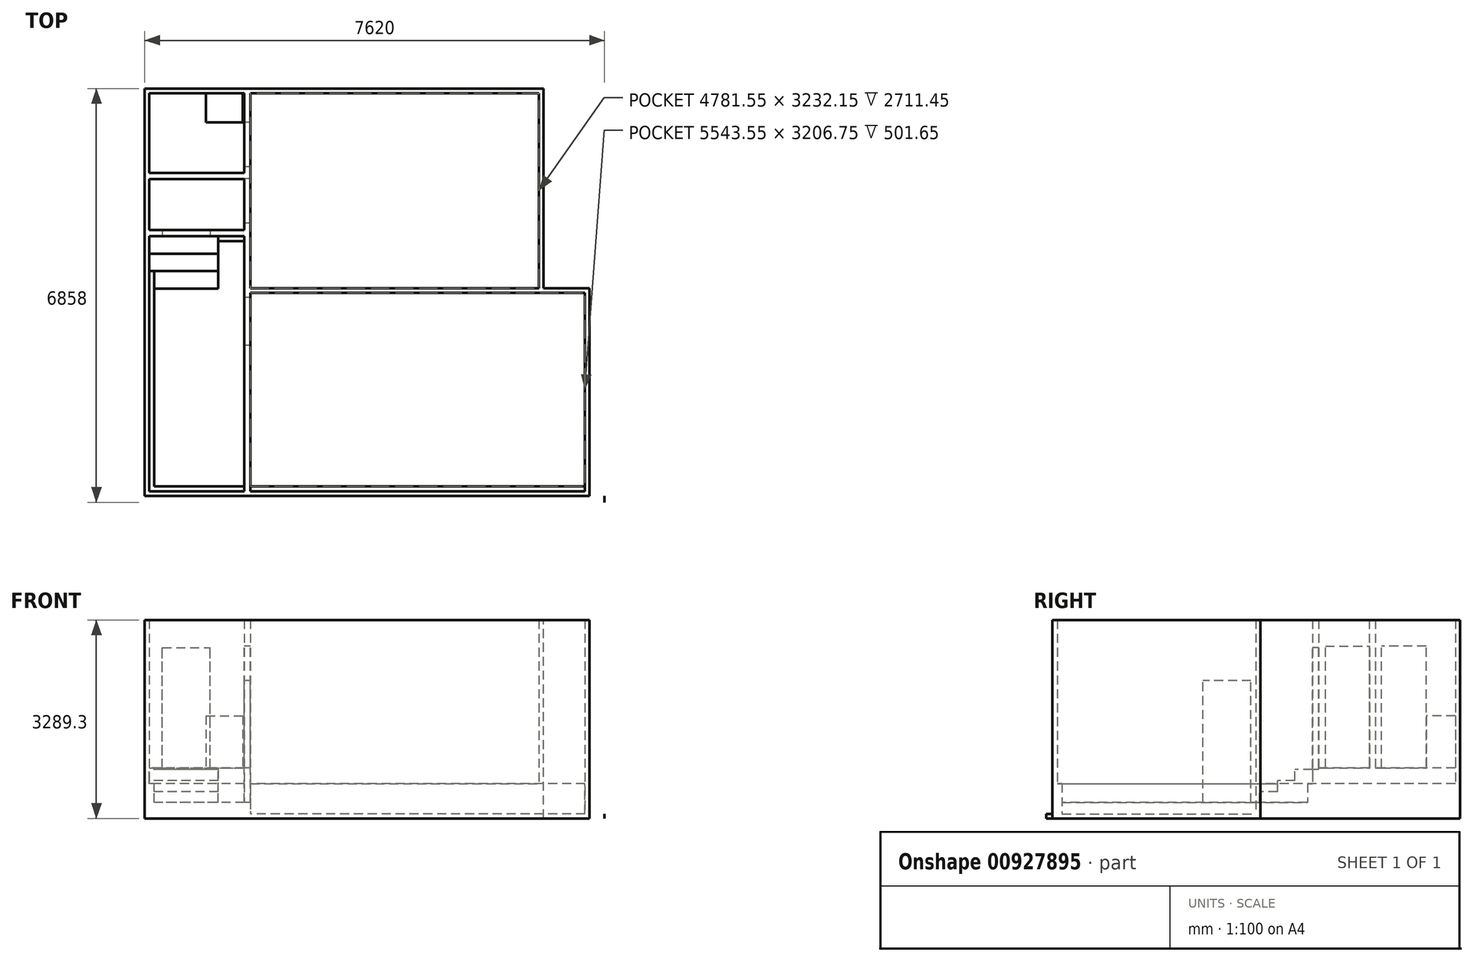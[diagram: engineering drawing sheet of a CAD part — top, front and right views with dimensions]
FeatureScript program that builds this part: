
annotation { "Feature Type Name" : "Feature", "Feature Type Description" : "" }
export const myFeature = defineFeature(function(context is Context, id is Id, definition is map)
    precondition{}
    {
        {
            var Q0;
            Q0=qCreatedBy(makeId("Top.planeOp"),FACE);
            var sketch = newSketch(context, id + "F0", { "sketchPlane" : qUnion([Q0])});
            skLineSegment(sketch, "E0.bottom", {"start": v(0, 0) * mm, "end": v(7620, 0) * mm});
            skLineSegment(sketch, "E0.top", {"start": v(0, -6858) * mm, "end": v(7620, -6858) * mm});
            skLineSegment(sketch, "E0.left", {"start": v(0, 0) * mm, "end": v(0, -6858) * mm});
            skLineSegment(sketch, "E0.right", {"start": v(7620, 0) * mm, "end": v(7620, -6858) * mm});
            skSolve(sketch);
        }
        {
            var Q0;
            Q0=makeQuery(id+"F0.imprint","IMPRINT",FACE,{"disambiguationData":[TD([[makeQuery(id+"F0.imprint","IMPRINT",EDGE,{"derivedFrom":sQuery(id+"F0.wireOp",EDGE,"E0.bottom")}),-1.0]])]});
            extrude(context, id + "F1", {"entities" : qUnion([Q0]), "oppositeDirection" : true, "depth" : 76.2 * mm, "offsetDistance" : 25.4 * mm});
        }
        {
            var Q0;
            Q0=makeQuery(id+"F1.opExtrude","CAP_FACE",FACE,{"disambiguationData":[OSD([sQuery(id+"F0.wireOp",EDGE,"E0.bottom"),sQuery(id+"F0.wireOp",EDGE,"E0.top"),sQuery(id+"F0.wireOp",EDGE,"E0.left"),sQuery(id+"F0.wireOp",EDGE,"E0.right")])],"isStart":true});
            var sketch = newSketch(context, id + "F2", { "sketchPlane" : qUnion([Q0])});
            skLineSegment(sketch, "E1.bottom", {"start": v(0, 0) * mm, "end": v(76.2, 0) * mm});
            skLineSegment(sketch, "E1.top", {"start": v(0, -6858) * mm, "end": v(76.2, -6858) * mm});
            skLineSegment(sketch, "E1.left", {"start": v(0, 0) * mm, "end": v(0, -6858) * mm});
            skLineSegment(sketch, "E1.right", {"start": v(76.2, 0) * mm, "end": v(76.2, -6858) * mm});
            skSolve(sketch);
        }
        {
            var Q0;
            Q0=qSketchRegion(id+"F2",true);
            extrude(context, id + "F3", {"entities" : qUnion([Q0]), "operationType" : NewBodyOperationType.ADD, "depth" : 3213.1 * mm, "offsetDistance" : 25.4 * mm});
        }
        {
            var Q0;
            Q0=makeQuery(id+"F1.opExtrude","CAP_FACE",FACE,{"disambiguationData":[OSD([sQuery(id+"F0.wireOp",EDGE,"E0.bottom"),sQuery(id+"F0.wireOp",EDGE,"E0.top"),sQuery(id+"F0.wireOp",EDGE,"E0.left"),sQuery(id+"F0.wireOp",EDGE,"E0.right")])],"isStart":true});
            var sketch = newSketch(context, id + "F4", { "sketchPlane" : qUnion([Q0])});
            skLineSegment(sketch, "E2.bottom", {"start": v(76.2, 0) * mm, "end": v(7620, 0) * mm});
            skLineSegment(sketch, "E2.top", {"start": v(76.2, -76.2) * mm, "end": v(7620, -76.2) * mm});
            skLineSegment(sketch, "E2.left", {"start": v(76.2, 0) * mm, "end": v(76.2, -76.2) * mm});
            skLineSegment(sketch, "E2.right", {"start": v(7620, 0) * mm, "end": v(7620, -76.2) * mm});
            skSolve(sketch);
        }
        {
            var Q0;
            Q0=qSketchRegion(id+"F4",true);
            extrude(context, id + "F5", {"entities" : qUnion([Q0]), "operationType" : NewBodyOperationType.ADD, "depth" : 3213.1 * mm, "offsetDistance" : 25.4 * mm});
        }
        {
            var Q0;
            Q0=makeQuery(id+"F1.opExtrude","CAP_FACE",FACE,{"disambiguationData":[OSD([sQuery(id+"F0.wireOp",EDGE,"E0.bottom"),sQuery(id+"F0.wireOp",EDGE,"E0.top"),sQuery(id+"F0.wireOp",EDGE,"E0.left"),sQuery(id+"F0.wireOp",EDGE,"E0.right")])],"isStart":true});
            var sketch = newSketch(context, id + "F6", { "sketchPlane" : qUnion([Q0])});
            skLineSegment(sketch, "E3.bottom", {"start": v(76.2, -76.2) * mm, "end": v(1752.6, -76.2) * mm});
            skLineSegment(sketch, "E3.top", {"start": v(76.2, -2444.75) * mm, "end": v(1752.6, -2444.75) * mm});
            skLineSegment(sketch, "E3.left", {"start": v(76.2, -76.2) * mm, "end": v(76.2, -2444.75) * mm});
            skLineSegment(sketch, "E3.right", {"start": v(1752.6, -76.2) * mm, "end": v(1752.6, -2444.75) * mm});
            skSolve(sketch);
        }
        {
            var Q0;
            Q0=makeQuery(id+"F6.imprint","IMPRINT",FACE,{"disambiguationData":[TD([[makeQuery(id+"F6.imprint","IMPRINT",EDGE,{"derivedFrom":sQuery(id+"F6.wireOp",EDGE,"E3.bottom")}),-1.0]])]});
            extrude(context, id + "F7", {"entities" : qUnion([Q0]), "operationType" : NewBodyOperationType.ADD, "depth" : 736.6 * mm, "offsetDistance" : 25.4 * mm});
        }
        {
            var Q0;
            Q0=makeQuery(id+"F7.opExtrude","CAP_FACE",FACE,{"disambiguationData":[OSD([sQuery(id+"F6.wireOp",EDGE,"E3.bottom"),sQuery(id+"F6.wireOp",EDGE,"E3.top"),sQuery(id+"F6.wireOp",EDGE,"E3.left"),sQuery(id+"F6.wireOp",EDGE,"E3.right")])],"isStart":false});
            var sketch = newSketch(context, id + "F8", { "sketchPlane" : qUnion([Q0])});
            skSolve(sketch);
        }
        {
            var Q0;
            Q0=makeQuery(id+"F8.imprint","IMPRINT",FACE,{"disambiguationData":[TD([[makeQuery(id+"F8.imprint","IMPRINT",EDGE,{"derivedFrom":makeQuery(id+"F7.opExtrude","CAP_EDGE",EDGE,{"disambiguationData":[OSD([sQuery(id+"F6.wireOp",EDGE,"E3.top")])],"isStart":false})}),1.0]])]});
            extrude(context, id + "F9", {"entities" : qUnion([Q0]), "operationType" : NewBodyOperationType.ADD, "depth" : 25.4 * mm, "offsetDistance" : 25.4 * mm});
        }
        {
            var Q0;
            Q0=makeQuery(id+"F9.opExtrude","CAP_FACE",FACE,{"disambiguationData":[OSD([sQuery(id+"F6.wireOp",EDGE,"E3.bottom"),sQuery(id+"F6.wireOp",EDGE,"E3.top"),sQuery(id+"F6.wireOp",EDGE,"E3.left"),sQuery(id+"F6.wireOp",EDGE,"E3.right")])],"isStart":false});
            var sketch = newSketch(context, id + "F10", { "sketchPlane" : qUnion([Q0])});
            skLineSegment(sketch, "E4.bottom", {"start": v(76.2, -2444.75) * mm, "end": v(1752.6, -2444.75) * mm});
            skLineSegment(sketch, "E4.top", {"start": v(76.2, -2343.15) * mm, "end": v(1752.6, -2343.15) * mm});
            skLineSegment(sketch, "E4.left", {"start": v(76.2, -2444.75) * mm, "end": v(76.2, -2343.15) * mm});
            skLineSegment(sketch, "E4.right", {"start": v(1752.6, -2444.75) * mm, "end": v(1752.6, -2343.15) * mm});
            skLineSegment(sketch, "E5.bottom", {"start": v(1752.6, -2343.15) * mm, "end": v(1651, -2343.15) * mm});
            skLineSegment(sketch, "E5.top", {"start": v(1752.6, -76.2) * mm, "end": v(1651, -76.2) * mm});
            skLineSegment(sketch, "E5.left", {"start": v(1752.6, -2343.15) * mm, "end": v(1752.6, -76.2) * mm});
            skLineSegment(sketch, "E5.right", {"start": v(1651, -2343.15) * mm, "end": v(1651, -76.2) * mm});
            skSolve(sketch);
        }
        {
            var Q0;
            Q0=qSketchRegion(id+"F10",true);
            extrude(context, id + "F11", {"entities" : qUnion([Q0]), "operationType" : NewBodyOperationType.ADD, "depth" : 2451.1 * mm, "offsetDistance" : 25.4 * mm});
        }
        {
            var Q0;
            {var subQ0=sQuery(id+"F2.wireOp",EDGE,"E1.right");var subQ2=sQuery(id+"F0.wireOp",EDGE,"E0.top");Q0=makeQuery(id+"F11.boolean.opBoolean","SPLIT",FACE,{"disambiguationData":[TD([makeQuery(id+"F1.opExtrude","SWEPT_FACE",FACE,{"disambiguationData":[OSD([subQ2])]})])],"derivedFrom":makeQuery(id+"F3.opExtrude","SWEPT_FACE",FACE,{"disambiguationData":[OSD([subQ0])]})});}
            var sketch = newSketch(context, id + "F12", { "sketchPlane" : qUnion([Q0])});
            skLineSegment(sketch, "E6.bottom", {"start": v(-2444.75, 0) * mm, "end": v(-2736.85, 0) * mm});
            skLineSegment(sketch, "E6.top", {"start": v(-2444.75, 736.6) * mm, "end": v(-2736.85, 736.6) * mm});
            skLineSegment(sketch, "E6.left", {"start": v(-2444.75, 0) * mm, "end": v(-2444.75, 736.6) * mm});
            skLineSegment(sketch, "E6.right", {"start": v(-2736.85, 552.45) * mm, "end": v(-2736.85, 736.6) * mm});
            skLineSegment(sketch, "E7.bottom", {"start": v(-2736.85, 0) * mm, "end": v(-3022.6, 0) * mm});
            skLineSegment(sketch, "E7.top", {"start": v(-2736.85, 552.45) * mm, "end": v(-3022.6, 552.45) * mm});
            skLineSegment(sketch, "E7.right", {"start": v(-3022.6, 368.3) * mm, "end": v(-3022.6, 552.45) * mm});
            skLineSegment(sketch, "E8.bottom", {"start": v(-3022.6, 0) * mm, "end": v(-3314.7, 0) * mm});
            skLineSegment(sketch, "E8.top", {"start": v(-3022.6, 368.3) * mm, "end": v(-3314.7, 368.3) * mm});
            skLineSegment(sketch, "E8.right", {"start": v(-3314.7, 184.15) * mm, "end": v(-3314.7, 368.3) * mm});
            skLineSegment(sketch, "E9.bottom", {"start": v(-3314.7, 0) * mm, "end": v(-3606.8, 0) * mm});
            skLineSegment(sketch, "E9.top", {"start": v(-3314.7, 184.15) * mm, "end": v(-3606.8, 184.15) * mm});
            skLineSegment(sketch, "E9.right", {"start": v(-3606.8, 0) * mm, "end": v(-3606.8, 184.15) * mm});
            skSolve(sketch);
        }
        {
            var Q0;
            Q0=makeQuery(id+"F12.imprint","IMPRINT",FACE,{"disambiguationData":[TD([[makeQuery(id+"F12.imprint","IMPRINT",EDGE,{"derivedFrom":sQuery(id+"F12.wireOp",EDGE,"E6.bottom")}),-1.0]])]});
            extrude(context, id + "F13", {"entities" : qUnion([Q0]), "operationType" : NewBodyOperationType.ADD, "depth" : 1143 * mm, "offsetDistance" : 25.4 * mm});
        }
        {
            var Q0;
            Q0=makeQuery(id+"F1.opExtrude","CAP_FACE",FACE,{"disambiguationData":[OSD([sQuery(id+"F0.wireOp",EDGE,"E0.bottom"),sQuery(id+"F0.wireOp",EDGE,"E0.top"),sQuery(id+"F0.wireOp",EDGE,"E0.left"),sQuery(id+"F0.wireOp",EDGE,"E0.right")])],"isStart":true});
            var sketch = newSketch(context, id + "F14", { "sketchPlane" : qUnion([Q0])});
            skLineSegment(sketch, "E10.bottom", {"start": v(6534.15, -76.2) * mm, "end": v(6610.35, -76.2) * mm});
            skLineSegment(sketch, "E10.top", {"start": v(6534.15, -3384.55) * mm, "end": v(6610.35, -3384.55) * mm});
            skLineSegment(sketch, "E10.left", {"start": v(6534.15, -76.2) * mm, "end": v(6534.15, -3384.55) * mm});
            skLineSegment(sketch, "E10.right", {"start": v(6610.35, -76.2) * mm, "end": v(6610.35, -3384.55) * mm});
            skSolve(sketch);
        }
        {
            var Q0;
            Q0=qSketchRegion(id+"F14",true);
            extrude(context, id + "F15", {"entities" : qUnion([Q0]), "operationType" : NewBodyOperationType.ADD, "depth" : 3213.1 * mm, "offsetDistance" : 25.4 * mm});
        }
        {
            var Q0;
            Q0=makeQuery(id+"F1.opExtrude","CAP_FACE",FACE,{"disambiguationData":[OSD([sQuery(id+"F0.wireOp",EDGE,"E0.bottom"),sQuery(id+"F0.wireOp",EDGE,"E0.top"),sQuery(id+"F0.wireOp",EDGE,"E0.left"),sQuery(id+"F0.wireOp",EDGE,"E0.right")])],"isStart":true});
            var sketch = newSketch(context, id + "F16", { "sketchPlane" : qUnion([Q0])});
            skLineSegment(sketch, "E11.bottom", {"start": v(6610.35, -3384.55) * mm, "end": v(7620, -3384.55) * mm});
            skLineSegment(sketch, "E11.top", {"start": v(6610.35, -3308.35) * mm, "end": v(7620, -3308.35) * mm});
            skLineSegment(sketch, "E11.left", {"start": v(6610.35, -3384.55) * mm, "end": v(6610.35, -3308.35) * mm});
            skLineSegment(sketch, "E11.right", {"start": v(7620, -3384.55) * mm, "end": v(7620, -3308.35) * mm});
            skSolve(sketch);
        }
        {
            var Q0;
            Q0=qSketchRegion(id+"F16",true);
            extrude(context, id + "F17", {"entities" : qUnion([Q0]), "operationType" : NewBodyOperationType.ADD, "depth" : 3213.1 * mm, "offsetDistance" : 25.4 * mm});
        }
        {
            var Q0;
            {var subQ1=sQuery(id+"F0.wireOp",EDGE,"E0.top");var subQ3=sQuery(id+"F0.wireOp",EDGE,"E0.right");Q0=makeQuery(id+"F17.boolean.opBoolean","SPLIT",FACE,{"disambiguationData":[TD([makeQuery(id+"F1.opExtrude","SWEPT_FACE",FACE,{"disambiguationData":[OSD([subQ1])]})])],"derivedFrom":makeQuery(id+"F1.opExtrude","CAP_FACE",FACE,{"disambiguationData":[OSD([sQuery(id+"F0.wireOp",EDGE,"E0.bottom"),subQ1,sQuery(id+"F0.wireOp",EDGE,"E0.left"),subQ3])],"isStart":true})});}
            var sketch = newSketch(context, id + "F18", { "sketchPlane" : qUnion([Q0])});
            skLineSegment(sketch, "E12.bottom", {"start": v(7296.15, -3384.55) * mm, "end": v(7372.35, -3384.55) * mm});
            skLineSegment(sketch, "E12.top", {"start": v(7296.15, -6858) * mm, "end": v(7372.35, -6858) * mm});
            skLineSegment(sketch, "E12.left", {"start": v(7296.15, -3384.55) * mm, "end": v(7296.15, -6858) * mm});
            skLineSegment(sketch, "E12.right", {"start": v(7372.35, -3384.55) * mm, "end": v(7372.35, -6858) * mm});
            skSolve(sketch);
        }
        {
            var Q0;
            Q0=qSketchRegion(id+"F18",true);
            extrude(context, id + "F19", {"entities" : qUnion([Q0]), "operationType" : NewBodyOperationType.ADD, "depth" : 3213.1 * mm, "offsetDistance" : 25.4 * mm});
        }
        {
            var Q0;
            {var subQ7=sQuery(id+"F0.wireOp",EDGE,"E0.top");var subQ8=makeQuery(id+"F1.opExtrude","SWEPT_FACE",FACE,{"disambiguationData":[OSD([subQ7])]});var subQ10=makeQuery(id+"F3.opExtrude","SWEPT_FACE",FACE,{"disambiguationData":[OSD([sQuery(id+"F2.wireOp",EDGE,"E1.right")])]});var subQ15=sQuery(id+"F0.wireOp",EDGE,"E0.right");Q0=makeQuery(id+"F19.boolean.opBoolean","SPLIT",FACE,{"disambiguationData":[TD([subQ10])],"derivedFrom":makeQuery(id+"F17.boolean.opBoolean","SPLIT",FACE,{"disambiguationData":[TD([subQ8])],"derivedFrom":makeQuery(id+"F1.opExtrude","CAP_FACE",FACE,{"disambiguationData":[OSD([sQuery(id+"F0.wireOp",EDGE,"E0.bottom"),subQ7,sQuery(id+"F0.wireOp",EDGE,"E0.left"),subQ15])],"isStart":true})})});}
            var sketch = newSketch(context, id + "F20", { "sketchPlane" : qUnion([Q0])});
            skLineSegment(sketch, "E13.bottom", {"start": v(7296.15, -6750.05) * mm, "end": v(76.2, -6750.05) * mm});
            skLineSegment(sketch, "E13.top", {"start": v(7296.15, -6673.85) * mm, "end": v(76.2, -6673.85) * mm});
            skLineSegment(sketch, "E13.left", {"start": v(7296.15, -6750.05) * mm, "end": v(7296.15, -6673.85) * mm});
            skLineSegment(sketch, "E13.right", {"start": v(76.2, -6750.05) * mm, "end": v(76.2, -6673.85) * mm});
            skSolve(sketch);
        }
        {
            var Q0;
            Q0=qSketchRegion(id+"F20",true);
            extrude(context, id + "F21", {"entities" : qUnion([Q0]), "operationType" : NewBodyOperationType.ADD, "depth" : 3213.1 * mm, "offsetDistance" : 25.4 * mm});
        }
        {
            var Q0;
            Q0=makeQuery(id+"F21.boolean.opBoolean","MERGE",FACE,{"derivedFrom":[makeQuery(id+"F19.boolean.opBoolean","MERGE",FACE,{"derivedFrom":[makeQuery(id+"F17.boolean.opBoolean","MERGE",FACE,{"derivedFrom":[makeQuery(id+"F15.boolean.opBoolean","MERGE",FACE,{"derivedFrom":[makeQuery(id+"F11.boolean.opBoolean","MERGE",FACE,{"derivedFrom":[makeQuery(id+"F5.boolean.opBoolean","MERGE",FACE,{"derivedFrom":[makeQuery(id+"F3.opExtrude","CAP_FACE",FACE,{"disambiguationData":[OSD([sQuery(id+"F2.wireOp",EDGE,"E1.bottom"),sQuery(id+"F2.wireOp",EDGE,"E1.top"),sQuery(id+"F2.wireOp",EDGE,"E1.left"),sQuery(id+"F2.wireOp",EDGE,"E1.right")])],"isStart":false}),makeQuery(id+"F5.opExtrude","CAP_FACE",FACE,{"disambiguationData":[OSD([sQuery(id+"F4.wireOp",EDGE,"E2.bottom"),sQuery(id+"F4.wireOp",EDGE,"E2.top"),sQuery(id+"F4.wireOp",EDGE,"E2.left"),sQuery(id+"F4.wireOp",EDGE,"E2.right")])],"isStart":false})]}),makeQuery(id+"F11.opExtrude","CAP_FACE",FACE,{"disambiguationData":[OSD([sQuery(id+"F10.wireOp",EDGE,"E4.bottom"),sQuery(id+"F10.wireOp",EDGE,"E4.top"),sQuery(id+"F10.wireOp",EDGE,"E4.left"),sQuery(id+"F10.wireOp",EDGE,"E4.right"),sQuery(id+"F10.wireOp",EDGE,"E5.top"),sQuery(id+"F10.wireOp",EDGE,"E5.left"),sQuery(id+"F10.wireOp",EDGE,"E5.right")])],"isStart":false})]}),makeQuery(id+"F15.opExtrude","CAP_FACE",FACE,{"disambiguationData":[OSD([sQuery(id+"F14.wireOp",EDGE,"E10.bottom"),sQuery(id+"F14.wireOp",EDGE,"E10.top"),sQuery(id+"F14.wireOp",EDGE,"E10.left"),sQuery(id+"F14.wireOp",EDGE,"E10.right")])],"isStart":false})]}),makeQuery(id+"F17.opExtrude","CAP_FACE",FACE,{"disambiguationData":[OSD([sQuery(id+"F16.wireOp",EDGE,"E11.bottom"),sQuery(id+"F16.wireOp",EDGE,"E11.top"),sQuery(id+"F16.wireOp",EDGE,"E11.left"),sQuery(id+"F16.wireOp",EDGE,"E11.right")])],"isStart":false})]}),makeQuery(id+"F19.opExtrude","CAP_FACE",FACE,{"disambiguationData":[OSD([sQuery(id+"F18.wireOp",EDGE,"E12.bottom"),sQuery(id+"F18.wireOp",EDGE,"E12.top"),sQuery(id+"F18.wireOp",EDGE,"E12.left"),sQuery(id+"F18.wireOp",EDGE,"E12.right")])],"isStart":false})]}),makeQuery(id+"F21.opExtrude","CAP_FACE",FACE,{"disambiguationData":[OSD([sQuery(id+"F20.wireOp",EDGE,"E13.bottom"),sQuery(id+"F20.wireOp",EDGE,"E13.top"),sQuery(id+"F20.wireOp",EDGE,"E13.left"),sQuery(id+"F20.wireOp",EDGE,"E13.right")])],"isStart":false})]});
            var sketch = newSketch(context, id + "F22", { "sketchPlane" : qUnion([Q0])});
            skLineSegment(sketch, "E14.bottom", {"start": v(0, -6858) * mm, "end": v(7614.91, -6858) * mm});
            skLineSegment(sketch, "E14.top", {"start": v(0, -6750.05) * mm, "end": v(7614.91, -6750.05) * mm});
            skLineSegment(sketch, "E14.left", {"start": v(0, -6858) * mm, "end": v(0, -6750.05) * mm});
            skLineSegment(sketch, "E14.right", {"start": v(7614.91, -6858) * mm, "end": v(7614.91, -6750.05) * mm});
            skSolve(sketch);
        }
        {
            var Q0;
            Q0=qSketchRegion(id+"F22",true);
            extrude(context, id + "F23", {"entities" : qUnion([Q0]), "operationType" : NewBodyOperationType.REMOVE, "oppositeDirection" : true, "depth" : 3289.3 * mm, "offsetDistance" : 25.4 * mm});
        }
        {
            var Q0;
            Q0=makeQuery(id+"F21.boolean.opBoolean","MERGE",FACE,{"derivedFrom":[makeQuery(id+"F19.boolean.opBoolean","MERGE",FACE,{"derivedFrom":[makeQuery(id+"F17.boolean.opBoolean","MERGE",FACE,{"derivedFrom":[makeQuery(id+"F15.boolean.opBoolean","MERGE",FACE,{"derivedFrom":[makeQuery(id+"F11.boolean.opBoolean","MERGE",FACE,{"derivedFrom":[makeQuery(id+"F5.boolean.opBoolean","MERGE",FACE,{"derivedFrom":[makeQuery(id+"F3.opExtrude","CAP_FACE",FACE,{"disambiguationData":[OSD([sQuery(id+"F2.wireOp",EDGE,"E1.bottom"),sQuery(id+"F2.wireOp",EDGE,"E1.top"),sQuery(id+"F2.wireOp",EDGE,"E1.left"),sQuery(id+"F2.wireOp",EDGE,"E1.right")])],"isStart":false}),makeQuery(id+"F5.opExtrude","CAP_FACE",FACE,{"disambiguationData":[OSD([sQuery(id+"F4.wireOp",EDGE,"E2.bottom"),sQuery(id+"F4.wireOp",EDGE,"E2.top"),sQuery(id+"F4.wireOp",EDGE,"E2.left"),sQuery(id+"F4.wireOp",EDGE,"E2.right")])],"isStart":false})]}),makeQuery(id+"F11.opExtrude","CAP_FACE",FACE,{"disambiguationData":[OSD([sQuery(id+"F10.wireOp",EDGE,"E4.bottom"),sQuery(id+"F10.wireOp",EDGE,"E4.top"),sQuery(id+"F10.wireOp",EDGE,"E4.left"),sQuery(id+"F10.wireOp",EDGE,"E4.right"),sQuery(id+"F10.wireOp",EDGE,"E5.top"),sQuery(id+"F10.wireOp",EDGE,"E5.left"),sQuery(id+"F10.wireOp",EDGE,"E5.right")])],"isStart":false})]}),makeQuery(id+"F15.opExtrude","CAP_FACE",FACE,{"disambiguationData":[OSD([sQuery(id+"F14.wireOp",EDGE,"E10.bottom"),sQuery(id+"F14.wireOp",EDGE,"E10.top"),sQuery(id+"F14.wireOp",EDGE,"E10.left"),sQuery(id+"F14.wireOp",EDGE,"E10.right")])],"isStart":false})]}),makeQuery(id+"F17.opExtrude","CAP_FACE",FACE,{"disambiguationData":[OSD([sQuery(id+"F16.wireOp",EDGE,"E11.bottom"),sQuery(id+"F16.wireOp",EDGE,"E11.top"),sQuery(id+"F16.wireOp",EDGE,"E11.left"),sQuery(id+"F16.wireOp",EDGE,"E11.right")])],"isStart":false})]}),makeQuery(id+"F19.opExtrude","CAP_FACE",FACE,{"disambiguationData":[OSD([sQuery(id+"F18.wireOp",EDGE,"E12.bottom"),sQuery(id+"F18.wireOp",EDGE,"E12.top"),sQuery(id+"F18.wireOp",EDGE,"E12.left"),sQuery(id+"F18.wireOp",EDGE,"E12.right")])],"isStart":false})]}),makeQuery(id+"F21.opExtrude","CAP_FACE",FACE,{"disambiguationData":[OSD([sQuery(id+"F20.wireOp",EDGE,"E13.bottom"),sQuery(id+"F20.wireOp",EDGE,"E13.top"),sQuery(id+"F20.wireOp",EDGE,"E13.left"),sQuery(id+"F20.wireOp",EDGE,"E13.right")])],"isStart":false})]});
            var sketch = newSketch(context, id + "F24", { "sketchPlane" : qUnion([Q0])});
            skLineSegment(sketch, "E15.bottom", {"start": v(7372.35, -6750.05) * mm, "end": v(7620, -6750.05) * mm});
            skLineSegment(sketch, "E15.top", {"start": v(7372.35, 0) * mm, "end": v(7620, 0) * mm});
            skLineSegment(sketch, "E15.left", {"start": v(7372.35, -6750.05) * mm, "end": v(7372.35, 0) * mm});
            skLineSegment(sketch, "E15.right", {"start": v(7620, -6750.05) * mm, "end": v(7620, 0) * mm});
            skSolve(sketch);
        }
        {
            var Q0;
            Q0=qSketchRegion(id+"F24",true);
            extrude(context, id + "F25", {"entities" : qUnion([Q0]), "operationType" : NewBodyOperationType.REMOVE, "oppositeDirection" : true, "depth" : 3289.3 * mm, "offsetDistance" : 25.4 * mm});
        }
        {
            var Q0;
            Q0=makeQuery(id+"F21.boolean.opBoolean","MERGE",FACE,{"derivedFrom":[makeQuery(id+"F19.boolean.opBoolean","MERGE",FACE,{"derivedFrom":[makeQuery(id+"F17.boolean.opBoolean","MERGE",FACE,{"derivedFrom":[makeQuery(id+"F15.boolean.opBoolean","MERGE",FACE,{"derivedFrom":[makeQuery(id+"F11.boolean.opBoolean","MERGE",FACE,{"derivedFrom":[makeQuery(id+"F5.boolean.opBoolean","MERGE",FACE,{"derivedFrom":[makeQuery(id+"F3.opExtrude","CAP_FACE",FACE,{"disambiguationData":[OSD([sQuery(id+"F2.wireOp",EDGE,"E1.bottom"),sQuery(id+"F2.wireOp",EDGE,"E1.top"),sQuery(id+"F2.wireOp",EDGE,"E1.left"),sQuery(id+"F2.wireOp",EDGE,"E1.right")])],"isStart":false}),makeQuery(id+"F5.opExtrude","CAP_FACE",FACE,{"disambiguationData":[OSD([sQuery(id+"F4.wireOp",EDGE,"E2.bottom"),sQuery(id+"F4.wireOp",EDGE,"E2.top"),sQuery(id+"F4.wireOp",EDGE,"E2.left"),sQuery(id+"F4.wireOp",EDGE,"E2.right")])],"isStart":false})]}),makeQuery(id+"F11.opExtrude","CAP_FACE",FACE,{"disambiguationData":[OSD([sQuery(id+"F10.wireOp",EDGE,"E4.bottom"),sQuery(id+"F10.wireOp",EDGE,"E4.top"),sQuery(id+"F10.wireOp",EDGE,"E4.left"),sQuery(id+"F10.wireOp",EDGE,"E4.right"),sQuery(id+"F10.wireOp",EDGE,"E5.top"),sQuery(id+"F10.wireOp",EDGE,"E5.left"),sQuery(id+"F10.wireOp",EDGE,"E5.right")])],"isStart":false})]}),makeQuery(id+"F15.opExtrude","CAP_FACE",FACE,{"disambiguationData":[OSD([sQuery(id+"F14.wireOp",EDGE,"E10.bottom"),sQuery(id+"F14.wireOp",EDGE,"E10.top"),sQuery(id+"F14.wireOp",EDGE,"E10.left"),sQuery(id+"F14.wireOp",EDGE,"E10.right")])],"isStart":false})]}),makeQuery(id+"F17.opExtrude","CAP_FACE",FACE,{"disambiguationData":[OSD([sQuery(id+"F16.wireOp",EDGE,"E11.bottom"),sQuery(id+"F16.wireOp",EDGE,"E11.top"),sQuery(id+"F16.wireOp",EDGE,"E11.left"),sQuery(id+"F16.wireOp",EDGE,"E11.right")])],"isStart":false})]}),makeQuery(id+"F19.opExtrude","CAP_FACE",FACE,{"disambiguationData":[OSD([sQuery(id+"F18.wireOp",EDGE,"E12.bottom"),sQuery(id+"F18.wireOp",EDGE,"E12.top"),sQuery(id+"F18.wireOp",EDGE,"E12.left"),sQuery(id+"F18.wireOp",EDGE,"E12.right")])],"isStart":false})]}),makeQuery(id+"F21.opExtrude","CAP_FACE",FACE,{"disambiguationData":[OSD([sQuery(id+"F20.wireOp",EDGE,"E13.bottom"),sQuery(id+"F20.wireOp",EDGE,"E13.top"),sQuery(id+"F20.wireOp",EDGE,"E13.left"),sQuery(id+"F20.wireOp",EDGE,"E13.right")])],"isStart":false})]});
            var sketch = newSketch(context, id + "F26", { "sketchPlane" : qUnion([Q0])});
            skLineSegment(sketch, "E16.bottom", {"start": v(6610.35, -3308.35) * mm, "end": v(7372.35, -3308.35) * mm});
            skLineSegment(sketch, "E16.top", {"start": v(6610.35, 0) * mm, "end": v(7372.35, 0) * mm});
            skLineSegment(sketch, "E16.left", {"start": v(6610.35, -3308.35) * mm, "end": v(6610.35, 0) * mm});
            skLineSegment(sketch, "E16.right", {"start": v(7372.35, -3308.35) * mm, "end": v(7372.35, 0) * mm});
            skSolve(sketch);
        }
        {
            var Q0;
            Q0=qSketchRegion(id+"F26",true);
            extrude(context, id + "F27", {"entities" : qUnion([Q0]), "operationType" : NewBodyOperationType.REMOVE, "oppositeDirection" : true, "depth" : 3289.3 * mm, "offsetDistance" : 25.4 * mm});
        }
        {
            var Q0;
            {var subQ0=sQuery(id+"F6.wireOp",EDGE,"E3.top");Q0=makeQuery(id+"F11.boolean.opBoolean","MERGE",FACE,{"derivedFrom":[makeQuery(id+"F9.boolean.opBoolean","MERGE",FACE,{"derivedFrom":[makeQuery(id+"F7.opExtrude","SWEPT_FACE",FACE,{"disambiguationData":[OSD([subQ0])]}),makeQuery(id+"F9.opExtrude","SWEPT_FACE",FACE,{"disambiguationData":[OSD([subQ0])]})]}),makeQuery(id+"F11.opExtrude","SWEPT_FACE",FACE,{"disambiguationData":[OSD([sQuery(id+"F10.wireOp",EDGE,"E4.bottom")])]})]});}
            var sketch = newSketch(context, id + "F28", { "sketchPlane" : qUnion([Q0])});
            skLineSegment(sketch, "E17.bottom", {"start": v(292.1, 736.6) * mm, "end": v(1085.85, 736.6) * mm});
            skLineSegment(sketch, "E17.top", {"start": v(292.1, 2755.9) * mm, "end": v(1085.85, 2755.9) * mm});
            skLineSegment(sketch, "E17.left", {"start": v(292.1, 736.6) * mm, "end": v(292.1, 2755.9) * mm});
            skLineSegment(sketch, "E17.right", {"start": v(1085.85, 736.6) * mm, "end": v(1085.85, 2755.9) * mm});
            skSolve(sketch);
        }
        {
            var Q0;
            Q0=qSketchRegion(id+"F28",true);
            extrude(context, id + "F29", {"entities" : qUnion([Q0]), "operationType" : NewBodyOperationType.REMOVE, "oppositeDirection" : true, "depth" : 101.6 * mm, "offsetDistance" : 25.4 * mm});
        }
        {
            var Q0;
            {var subQ0=sQuery(id+"F6.wireOp",EDGE,"E3.right");Q0=makeQuery(id+"F11.boolean.opBoolean","MERGE",FACE,{"derivedFrom":[makeQuery(id+"F9.boolean.opBoolean","MERGE",FACE,{"derivedFrom":[makeQuery(id+"F7.opExtrude","SWEPT_FACE",FACE,{"disambiguationData":[OSD([subQ0])]}),makeQuery(id+"F9.opExtrude","SWEPT_FACE",FACE,{"disambiguationData":[OSD([subQ0])]})]}),makeQuery(id+"F11.opExtrude","SWEPT_FACE",FACE,{"disambiguationData":[OSD([sQuery(id+"F10.wireOp",EDGE,"E4.right"),sQuery(id+"F10.wireOp",EDGE,"E5.left")])]})]});}
            var sketch = newSketch(context, id + "F30", { "sketchPlane" : qUnion([Q0])});
            skLineSegment(sketch, "E18.bottom", {"start": v(-76.2, 0) * mm, "end": v(-158.75, 0) * mm});
            skLineSegment(sketch, "E18.top", {"start": v(-76.2, 501.65) * mm, "end": v(-158.75, 501.65) * mm});
            skLineSegment(sketch, "E18.left", {"start": v(-76.2, 0) * mm, "end": v(-76.2, 501.65) * mm});
            skLineSegment(sketch, "E18.right", {"start": v(-158.75, 0) * mm, "end": v(-158.75, 501.65) * mm});
            skSolve(sketch);
        }
        {
            var Q0;
            Q0=qSketchRegion(id+"F30",true);
            var Q1;
            Q1=makeQuery(id+"F15.opExtrude","SWEPT_FACE",FACE,{"disambiguationData":[OSD([sQuery(id+"F14.wireOp",EDGE,"E10.left")])]});
            extrude(context, id + "F31", {"entities" : qUnion([Q0, Q1]), "operationType" : NewBodyOperationType.ADD, "endBound" : BoundingType.UP_TO_NEXT, "depth" : 25.4 * mm, "offsetDistance" : 25.4 * mm});
        }
        {
            var Q0;
            {var subQ0=sQuery(id+"F2.wireOp",EDGE,"E1.right");var subQ5=sQuery(id+"F6.wireOp",EDGE,"E3.top");var subQ6=makeQuery(id+"F7.opExtrude","SWEPT_FACE",FACE,{"disambiguationData":[OSD([subQ5])]});var subQ9=sQuery(id+"F0.wireOp",EDGE,"E0.top");Q0=makeQuery(id+"F21.boolean.opBoolean","SPLIT",FACE,{"disambiguationData":[TD([subQ6])],"derivedFrom":makeQuery(id+"F11.boolean.opBoolean","SPLIT",FACE,{"disambiguationData":[TD([makeQuery(id+"F1.opExtrude","SWEPT_FACE",FACE,{"disambiguationData":[OSD([subQ9])]})])],"derivedFrom":makeQuery(id+"F3.opExtrude","SWEPT_FACE",FACE,{"disambiguationData":[OSD([subQ0])]})})});}
            var sketch = newSketch(context, id + "F32", { "sketchPlane" : qUnion([Q0])});
            skLineSegment(sketch, "E19.bottom", {"start": v(-6673.85, 0) * mm, "end": v(-2609.85, 0) * mm});
            skLineSegment(sketch, "E19.top", {"start": v(-6673.85, 501.65) * mm, "end": v(-2609.85, 501.65) * mm});
            skLineSegment(sketch, "E19.left", {"start": v(-6673.85, 0) * mm, "end": v(-6673.85, 501.65) * mm});
            skLineSegment(sketch, "E19.right", {"start": v(-2609.85, 0) * mm, "end": v(-2609.85, 501.65) * mm});
            skSolve(sketch);
        }
        {
            var Q0;
            Q0=qSketchRegion(id+"F32",true);
            extrude(context, id + "F33", {"entities" : qUnion([Q0]), "operationType" : NewBodyOperationType.ADD, "depth" : 82.55 * mm, "offsetDistance" : 25.4 * mm});
        }
        {
            var Q0;
            Q0=makeQuery(id+"F31.opExtrude","SWEPT_FACE",FACE,{"disambiguationData":[OSD([sQuery(id+"F30.wireOp",EDGE,"E18.right")])]});
            var sketch = newSketch(context, id + "F34", { "sketchPlane" : qUnion([Q0])});
            skLineSegment(sketch, "E20.bottom", {"start": v(1752.6, 0) * mm, "end": v(1835.15, 0) * mm});
            skLineSegment(sketch, "E20.top", {"start": v(1752.6, 501.65) * mm, "end": v(1835.15, 501.65) * mm});
            skLineSegment(sketch, "E20.left", {"start": v(1752.6, 0) * mm, "end": v(1752.6, 501.65) * mm});
            skLineSegment(sketch, "E20.right", {"start": v(1835.15, 0) * mm, "end": v(1835.15, 501.65) * mm});
            skSolve(sketch);
        }
        {
            var Q0;
            Q0=qSketchRegion(id+"F34",true);
            var Q1;
            {var subQ0=sQuery(id+"F6.wireOp",EDGE,"E3.top");Q1=makeQuery(id+"F11.boolean.opBoolean","MERGE",FACE,{"derivedFrom":[makeQuery(id+"F9.boolean.opBoolean","MERGE",FACE,{"derivedFrom":[makeQuery(id+"F7.opExtrude","SWEPT_FACE",FACE,{"disambiguationData":[OSD([subQ0])]}),makeQuery(id+"F9.opExtrude","SWEPT_FACE",FACE,{"disambiguationData":[OSD([subQ0])]})]}),makeQuery(id+"F11.opExtrude","SWEPT_FACE",FACE,{"disambiguationData":[OSD([sQuery(id+"F10.wireOp",EDGE,"E4.bottom")])]})]});}
            extrude(context, id + "F35", {"entities" : qUnion([Q0]), "operationType" : NewBodyOperationType.ADD, "endBound" : BoundingType.UP_TO_SURFACE, "depth" : 25.4 * mm, "endBoundEntityFace" : qUnion([Q1]), "offsetDistance" : 25.4 * mm});
        }
        {
            var Q0;
            Q0=makeQuery(id+"F13.opExtrude","CAP_FACE",FACE,{"disambiguationData":[OSD([sQuery(id+"F12.wireOp",EDGE,"E6.bottom"),sQuery(id+"F12.wireOp",EDGE,"E6.top"),sQuery(id+"F12.wireOp",EDGE,"E6.left"),sQuery(id+"F12.wireOp",EDGE,"E6.right"),sQuery(id+"F12.wireOp",EDGE,"E7.bottom"),sQuery(id+"F12.wireOp",EDGE,"E7.top"),sQuery(id+"F12.wireOp",EDGE,"E7.right"),sQuery(id+"F12.wireOp",EDGE,"E8.bottom"),sQuery(id+"F12.wireOp",EDGE,"E8.top"),sQuery(id+"F12.wireOp",EDGE,"E8.right"),sQuery(id+"F12.wireOp",EDGE,"E9.bottom"),sQuery(id+"F12.wireOp",EDGE,"E9.top"),sQuery(id+"F12.wireOp",EDGE,"E9.right")])],"isStart":false});
            var sketch = newSketch(context, id + "F36", { "sketchPlane" : qUnion([Q0])});
            skLineSegment(sketch, "E21.bottom", {"start": v(-2444.75, 0) * mm, "end": v(-2527.3, 0) * mm});
            skLineSegment(sketch, "E21.top", {"start": v(-2444.75, 501.65) * mm, "end": v(-2527.3, 501.65) * mm});
            skLineSegment(sketch, "E21.left", {"start": v(-2444.75, 0) * mm, "end": v(-2444.75, 501.65) * mm});
            skLineSegment(sketch, "E21.right", {"start": v(-2527.3, 0) * mm, "end": v(-2527.3, 501.65) * mm});
            skSolve(sketch);
        }
        {
            var Q0;
            Q0=qSketchRegion(id+"F36",true);
            var Q1;
            Q1=makeQuery(id+"F35.opExtrude","SWEPT_FACE",FACE,{"disambiguationData":[OSD([sQuery(id+"F34.wireOp",EDGE,"E20.right")])]});
            extrude(context, id + "F37", {"entities" : qUnion([Q0]), "operationType" : NewBodyOperationType.ADD, "endBound" : BoundingType.UP_TO_SURFACE, "depth" : 25.4 * mm, "endBoundEntityFace" : qUnion([Q1]), "offsetDistance" : 25.4 * mm});
        }
        {
            var Q0;
            Q0=makeQuery(id+"F33.opExtrude","CAP_FACE",FACE,{"disambiguationData":[OSD([sQuery(id+"F32.wireOp",EDGE,"E19.bottom"),sQuery(id+"F32.wireOp",EDGE,"E19.top"),sQuery(id+"F32.wireOp",EDGE,"E19.left"),sQuery(id+"F32.wireOp",EDGE,"E19.right")])],"isStart":false});
            var sketch = newSketch(context, id + "F38", { "sketchPlane" : qUnion([Q0])});
            skLineSegment(sketch, "E22.bottom", {"start": v(-6673.85, 0) * mm, "end": v(-6591.3, 0) * mm});
            skLineSegment(sketch, "E22.top", {"start": v(-6673.85, 501.65) * mm, "end": v(-6591.3, 501.65) * mm});
            skLineSegment(sketch, "E22.left", {"start": v(-6673.85, 0) * mm, "end": v(-6673.85, 501.65) * mm});
            skLineSegment(sketch, "E22.right", {"start": v(-6591.3, 0) * mm, "end": v(-6591.3, 501.65) * mm});
            skSolve(sketch);
        }
        {
            var Q0;
            Q0=qSketchRegion(id+"F38",true);
            extrude(context, id + "F39", {"entities" : qUnion([Q0]), "operationType" : NewBodyOperationType.ADD, "endBound" : BoundingType.UP_TO_NEXT, "depth" : 25.4 * mm, "offsetDistance" : 25.4 * mm});
        }
        {
            var Q0;
            {var subQ8=makeQuery(id+"F3.opExtrude","SWEPT_FACE",FACE,{"disambiguationData":[OSD([sQuery(id+"F2.wireOp",EDGE,"E1.right")])]});var subQ9=makeQuery(id+"F5.opExtrude","SWEPT_FACE",FACE,{"disambiguationData":[OSD([sQuery(id+"F4.wireOp",EDGE,"E2.top")])]});var subQ17=sQuery(id+"F0.wireOp",EDGE,"E0.top");var subQ18=makeQuery(id+"F1.opExtrude","SWEPT_FACE",FACE,{"disambiguationData":[OSD([subQ17])]});var subQ20=sQuery(id+"F0.wireOp",EDGE,"E0.right");Q0=makeQuery(id+"F21.boolean.opBoolean","SPLIT",FACE,{"disambiguationData":[TD([subQ9])],"derivedFrom":makeQuery(id+"F19.boolean.opBoolean","SPLIT",FACE,{"disambiguationData":[TD([subQ8])],"derivedFrom":makeQuery(id+"F17.boolean.opBoolean","SPLIT",FACE,{"disambiguationData":[TD([subQ18])],"derivedFrom":makeQuery(id+"F1.opExtrude","CAP_FACE",FACE,{"disambiguationData":[OSD([sQuery(id+"F0.wireOp",EDGE,"E0.bottom"),subQ17,sQuery(id+"F0.wireOp",EDGE,"E0.left"),subQ20])],"isStart":true})})})});}
            var sketch = newSketch(context, id + "F40", { "sketchPlane" : qUnion([Q0])});
            skLineSegment(sketch, "E23.bottom", {"start": v(76.2, -6673.85) * mm, "end": v(1752.6, -6673.85) * mm});
            skLineSegment(sketch, "E23.top", {"start": v(76.2, -2444.75) * mm, "end": v(1752.6, -2444.75) * mm});
            skLineSegment(sketch, "E23.left", {"start": v(76.2, -6673.85) * mm, "end": v(76.2, -2444.75) * mm});
            skLineSegment(sketch, "E23.right", {"start": v(1752.6, -6673.85) * mm, "end": v(1752.6, -2444.75) * mm});
            skLineSegment(sketch, "E24.bottom", {"start": v(6534.15, -3384.55) * mm, "end": v(1752.6, -3384.55) * mm});
            skLineSegment(sketch, "E24.top", {"start": v(6534.15, -76.2) * mm, "end": v(1752.6, -76.2) * mm});
            skLineSegment(sketch, "E24.left", {"start": v(6534.15, -3384.55) * mm, "end": v(6534.15, -76.2) * mm});
            skLineSegment(sketch, "E24.right", {"start": v(1752.6, -3384.55) * mm, "end": v(1752.6, -76.2) * mm});
            skSolve(sketch);
        }
        {
            var Q0;
            Q0 = qSketchRegion(id + "F40", true);
            extrude(context, id + "F41", {"entities" : qUnion([Q0]), "operationType" : NewBodyOperationType.ADD, "depth" : 190.5 * mm, "offsetDistance" : 25.4 * mm});
        }
        {
            var Q0;
            Q0=makeQuery(id+"F41.opExtrude","CAP_FACE",FACE,{"disambiguationData":[OSD([sQuery(id+"F40.wireOp",EDGE,"E23.bottom"),sQuery(id+"F40.wireOp",EDGE,"E23.top"),sQuery(id+"F40.wireOp",EDGE,"E23.left"),sQuery(id+"F40.wireOp",EDGE,"E23.right"),sQuery(id+"F40.wireOp",EDGE,"E24.bottom"),sQuery(id+"F40.wireOp",EDGE,"E24.top"),sQuery(id+"F40.wireOp",EDGE,"E24.left"),sQuery(id+"F40.wireOp",EDGE,"E24.right")])],"isStart":false});
            var sketch = newSketch(context, id + "F42", { "sketchPlane" : qUnion([Q0])});
            skLineSegment(sketch, "E25.bottom", {"start": v(1752.6, -3384.55) * mm, "end": v(1651, -3384.55) * mm});
            skLineSegment(sketch, "E25.top", {"start": v(1752.6, -2444.75) * mm, "end": v(1651, -2444.75) * mm});
            skLineSegment(sketch, "E25.left", {"start": v(1752.6, -3384.55) * mm, "end": v(1752.6, -2444.75) * mm});
            skLineSegment(sketch, "E25.right", {"start": v(1651, -3384.55) * mm, "end": v(1651, -2444.75) * mm});
            skSolve(sketch);
        }
        {
            var Q0;
            Q0 = qSketchRegion(id + "F42", true);
            var Q1;
            Q1=makeQuery(id+"F21.boolean.opBoolean","MERGE",FACE,{"derivedFrom":[makeQuery(id+"F19.boolean.opBoolean","MERGE",FACE,{"derivedFrom":[makeQuery(id+"F17.boolean.opBoolean","MERGE",FACE,{"derivedFrom":[makeQuery(id+"F15.boolean.opBoolean","MERGE",FACE,{"derivedFrom":[makeQuery(id+"F11.boolean.opBoolean","MERGE",FACE,{"derivedFrom":[makeQuery(id+"F5.boolean.opBoolean","MERGE",FACE,{"derivedFrom":[makeQuery(id+"F3.opExtrude","CAP_FACE",FACE,{"disambiguationData":[OSD([sQuery(id+"F2.wireOp",EDGE,"E1.bottom"),sQuery(id+"F2.wireOp",EDGE,"E1.top"),sQuery(id+"F2.wireOp",EDGE,"E1.left"),sQuery(id+"F2.wireOp",EDGE,"E1.right")])],"isStart":false}),makeQuery(id+"F5.opExtrude","CAP_FACE",FACE,{"disambiguationData":[OSD([sQuery(id+"F4.wireOp",EDGE,"E2.bottom"),sQuery(id+"F4.wireOp",EDGE,"E2.top"),sQuery(id+"F4.wireOp",EDGE,"E2.left"),sQuery(id+"F4.wireOp",EDGE,"E2.right")])],"isStart":false})]}),makeQuery(id+"F11.opExtrude","CAP_FACE",FACE,{"disambiguationData":[OSD([sQuery(id+"F10.wireOp",EDGE,"E4.bottom"),sQuery(id+"F10.wireOp",EDGE,"E4.top"),sQuery(id+"F10.wireOp",EDGE,"E4.left"),sQuery(id+"F10.wireOp",EDGE,"E4.right"),sQuery(id+"F10.wireOp",EDGE,"E5.top"),sQuery(id+"F10.wireOp",EDGE,"E5.left"),sQuery(id+"F10.wireOp",EDGE,"E5.right")])],"isStart":false})]}),makeQuery(id+"F15.opExtrude","CAP_FACE",FACE,{"disambiguationData":[OSD([sQuery(id+"F14.wireOp",EDGE,"E10.bottom"),sQuery(id+"F14.wireOp",EDGE,"E10.top"),sQuery(id+"F14.wireOp",EDGE,"E10.left"),sQuery(id+"F14.wireOp",EDGE,"E10.right")])],"isStart":false})]}),makeQuery(id+"F17.opExtrude","CAP_FACE",FACE,{"disambiguationData":[OSD([sQuery(id+"F16.wireOp",EDGE,"E11.bottom"),sQuery(id+"F16.wireOp",EDGE,"E11.top"),sQuery(id+"F16.wireOp",EDGE,"E11.left"),sQuery(id+"F16.wireOp",EDGE,"E11.right")])],"isStart":false})]}),makeQuery(id+"F19.opExtrude","CAP_FACE",FACE,{"disambiguationData":[OSD([sQuery(id+"F18.wireOp",EDGE,"E12.bottom"),sQuery(id+"F18.wireOp",EDGE,"E12.top"),sQuery(id+"F18.wireOp",EDGE,"E12.left"),sQuery(id+"F18.wireOp",EDGE,"E12.right")])],"isStart":false})]}),makeQuery(id+"F21.opExtrude","CAP_FACE",FACE,{"disambiguationData":[OSD([sQuery(id+"F20.wireOp",EDGE,"E13.bottom"),sQuery(id+"F20.wireOp",EDGE,"E13.top"),sQuery(id+"F20.wireOp",EDGE,"E13.left"),sQuery(id+"F20.wireOp",EDGE,"E13.right")])],"isStart":false})]});
            extrude(context, id + "F43", {"entities" : qUnion([Q0]), "operationType" : NewBodyOperationType.ADD, "endBound" : BoundingType.UP_TO_SURFACE, "depth" : 25.4 * mm, "endBoundEntityFace" : qUnion([Q1]), "offsetDistance" : 25.4 * mm});
        }
        {
            var Q0;
            {var subQ2=sQuery(id+"F40.wireOp",EDGE,"E24.bottom");var subQ3=sQuery(id+"F40.wireOp",EDGE,"E23.right");var subQ4=makeQuery(id+"F41.opExtrude","CAP_FACE",FACE,{"disambiguationData":[OSD([sQuery(id+"F40.wireOp",EDGE,"E23.bottom"),sQuery(id+"F40.wireOp",EDGE,"E23.top"),sQuery(id+"F40.wireOp",EDGE,"E23.left"),subQ3,subQ2,sQuery(id+"F40.wireOp",EDGE,"E24.top"),sQuery(id+"F40.wireOp",EDGE,"E24.left"),sQuery(id+"F40.wireOp",EDGE,"E24.right")])],"isStart":false});Q0=makeQuery(id+"F43.boolean.opBoolean","SPLIT",FACE,{"disambiguationData":[TD([makeQuery(id+"F15.opExtrude","SWEPT_FACE",FACE,{"disambiguationData":[OSD([sQuery(id+"F14.wireOp",EDGE,"E10.left")])]})])],"derivedFrom":subQ4});}
            var Q1;
            {var subQ2=sQuery(id+"F36.wireOp",EDGE,"E21.top");Q1=makeQuery(id+"F43.boolean.opBoolean","SPLIT",FACE,{"disambiguationData":[TD([makeQuery(id+"F5.opExtrude","SWEPT_FACE",FACE,{"disambiguationData":[OSD([sQuery(id+"F4.wireOp",EDGE,"E2.top")])]})])],"derivedFrom":makeQuery(id+"F37.boolean.opBoolean","MERGE",FACE,{"derivedFrom":[makeQuery(id+"F35.boolean.opBoolean","MERGE",FACE,{"derivedFrom":[makeQuery(id+"F31.opExtrude","SWEPT_FACE",FACE,{"disambiguationData":[OSD([sQuery(id+"F30.wireOp",EDGE,"E18.top")])]}),makeQuery(id+"F35.opExtrude","SWEPT_FACE",FACE,{"disambiguationData":[OSD([sQuery(id+"F34.wireOp",EDGE,"E20.top")])]})]}),makeQuery(id+"F37.opExtrude","SWEPT_FACE",FACE,{"disambiguationData":[OSD([subQ2])]})]})});}
            extrude(context, id + "F44", {"entities" : qUnion([Q0]), "operationType" : NewBodyOperationType.ADD, "endBound" : BoundingType.UP_TO_SURFACE, "depth" : 25.4 * mm, "endBoundEntityFace" : qUnion([Q1]), "offsetDistance" : 25.4 * mm});
        }
        {
            var Q0;
            {var subQ1=sQuery(id+"F12.wireOp",EDGE,"E8.right");var subQ2=sQuery(id+"F40.wireOp",EDGE,"E24.bottom");var subQ3=sQuery(id+"F40.wireOp",EDGE,"E23.right");var subQ4=makeQuery(id+"F41.opExtrude","CAP_FACE",FACE,{"disambiguationData":[OSD([sQuery(id+"F40.wireOp",EDGE,"E23.bottom"),sQuery(id+"F40.wireOp",EDGE,"E23.top"),sQuery(id+"F40.wireOp",EDGE,"E23.left"),subQ3,subQ2,sQuery(id+"F40.wireOp",EDGE,"E24.top"),sQuery(id+"F40.wireOp",EDGE,"E24.left"),sQuery(id+"F40.wireOp",EDGE,"E24.right")])],"isStart":false});Q0=makeQuery(id+"F43.boolean.opBoolean","SPLIT",FACE,{"disambiguationData":[TD([makeQuery(id+"F13.opExtrude","SWEPT_FACE",FACE,{"disambiguationData":[OSD([subQ1])]})])],"derivedFrom":subQ4});}
            var sketch = newSketch(context, id + "F45", { "sketchPlane" : qUnion([Q0])});
            skLineSegment(sketch, "E26.bottom", {"start": v(1651, -3384.55) * mm, "end": v(1752.6, -3384.55) * mm});
            skLineSegment(sketch, "E26.top", {"start": v(1651, -6591.3) * mm, "end": v(1752.6, -6591.3) * mm});
            skLineSegment(sketch, "E26.left", {"start": v(1651, -3384.55) * mm, "end": v(1651, -6591.3) * mm});
            skLineSegment(sketch, "E26.right", {"start": v(1752.6, -3384.55) * mm, "end": v(1752.6, -6591.3) * mm});
            skSolve(sketch);
        }
        {
            var Q0;
            Q0 = qSketchRegion(id + "F45", true);
            var Q1;
            Q1=makeQuery(id+"F43.boolean.opBoolean","MERGE",FACE,{"derivedFrom":[makeQuery(id+"F21.boolean.opBoolean","MERGE",FACE,{"derivedFrom":[makeQuery(id+"F19.boolean.opBoolean","MERGE",FACE,{"derivedFrom":[makeQuery(id+"F17.boolean.opBoolean","MERGE",FACE,{"derivedFrom":[makeQuery(id+"F15.boolean.opBoolean","MERGE",FACE,{"derivedFrom":[makeQuery(id+"F11.boolean.opBoolean","MERGE",FACE,{"derivedFrom":[makeQuery(id+"F5.boolean.opBoolean","MERGE",FACE,{"derivedFrom":[makeQuery(id+"F3.opExtrude","CAP_FACE",FACE,{"disambiguationData":[OSD([sQuery(id+"F2.wireOp",EDGE,"E1.bottom"),sQuery(id+"F2.wireOp",EDGE,"E1.top"),sQuery(id+"F2.wireOp",EDGE,"E1.left"),sQuery(id+"F2.wireOp",EDGE,"E1.right")])],"isStart":false}),makeQuery(id+"F5.opExtrude","CAP_FACE",FACE,{"disambiguationData":[OSD([sQuery(id+"F4.wireOp",EDGE,"E2.bottom"),sQuery(id+"F4.wireOp",EDGE,"E2.top"),sQuery(id+"F4.wireOp",EDGE,"E2.left"),sQuery(id+"F4.wireOp",EDGE,"E2.right")])],"isStart":false})]}),makeQuery(id+"F11.opExtrude","CAP_FACE",FACE,{"disambiguationData":[OSD([sQuery(id+"F10.wireOp",EDGE,"E4.bottom"),sQuery(id+"F10.wireOp",EDGE,"E4.top"),sQuery(id+"F10.wireOp",EDGE,"E4.left"),sQuery(id+"F10.wireOp",EDGE,"E4.right"),sQuery(id+"F10.wireOp",EDGE,"E5.top"),sQuery(id+"F10.wireOp",EDGE,"E5.left"),sQuery(id+"F10.wireOp",EDGE,"E5.right")])],"isStart":false})]}),makeQuery(id+"F15.opExtrude","CAP_FACE",FACE,{"disambiguationData":[OSD([sQuery(id+"F14.wireOp",EDGE,"E10.bottom"),sQuery(id+"F14.wireOp",EDGE,"E10.top"),sQuery(id+"F14.wireOp",EDGE,"E10.left"),sQuery(id+"F14.wireOp",EDGE,"E10.right")])],"isStart":false})]}),makeQuery(id+"F17.opExtrude","CAP_FACE",FACE,{"disambiguationData":[OSD([sQuery(id+"F16.wireOp",EDGE,"E11.bottom"),sQuery(id+"F16.wireOp",EDGE,"E11.top"),sQuery(id+"F16.wireOp",EDGE,"E11.left"),sQuery(id+"F16.wireOp",EDGE,"E11.right")])],"isStart":false})]}),makeQuery(id+"F19.opExtrude","CAP_FACE",FACE,{"disambiguationData":[OSD([sQuery(id+"F18.wireOp",EDGE,"E12.bottom"),sQuery(id+"F18.wireOp",EDGE,"E12.top"),sQuery(id+"F18.wireOp",EDGE,"E12.left"),sQuery(id+"F18.wireOp",EDGE,"E12.right")])],"isStart":false})]}),makeQuery(id+"F21.opExtrude","CAP_FACE",FACE,{"disambiguationData":[OSD([sQuery(id+"F20.wireOp",EDGE,"E13.bottom"),sQuery(id+"F20.wireOp",EDGE,"E13.top"),sQuery(id+"F20.wireOp",EDGE,"E13.left"),sQuery(id+"F20.wireOp",EDGE,"E13.right")])],"isStart":false})]}),makeQuery(id+"F43.opExtrude","CAP_FACE",FACE,{"disambiguationData":[OSD([sQuery(id+"F42.wireOp",EDGE,"E25.bottom"),sQuery(id+"F42.wireOp",EDGE,"E25.top"),sQuery(id+"F42.wireOp",EDGE,"E25.left"),sQuery(id+"F42.wireOp",EDGE,"E25.right")])],"isStart":false})]});
            extrude(context, id + "F46", {"entities" : qUnion([Q0]), "operationType" : NewBodyOperationType.ADD, "endBound" : BoundingType.UP_TO_SURFACE, "depth" : 25.4 * mm, "endBoundEntityFace" : qUnion([Q1]), "offsetDistance" : 25.4 * mm});
        }
        {
            var Q0;
            Q0=makeQuery(id+"F39.boolean.opBoolean","MERGE",FACE,{"derivedFrom":[makeQuery(id+"F33.opExtrude","SWEPT_FACE",FACE,{"disambiguationData":[OSD([sQuery(id+"F32.wireOp",EDGE,"E19.top")])]}),makeQuery(id+"F39.opExtrude","SWEPT_FACE",FACE,{"disambiguationData":[OSD([sQuery(id+"F38.wireOp",EDGE,"E22.top")])]})]});
            var sketch = newSketch(context, id + "F47", { "sketchPlane" : qUnion([Q0])});
            skLineSegment(sketch, "E27.bottom", {"start": v(1651, -6591.3) * mm, "end": v(1752.6, -6591.3) * mm});
            skLineSegment(sketch, "E27.top", {"start": v(1651, -6673.85) * mm, "end": v(1752.6, -6673.85) * mm});
            skLineSegment(sketch, "E27.left", {"start": v(1651, -6591.3) * mm, "end": v(1651, -6673.85) * mm});
            skLineSegment(sketch, "E27.right", {"start": v(1752.6, -6591.3) * mm, "end": v(1752.6, -6673.85) * mm});
            skSolve(sketch);
        }
        {
            var Q0;
            Q0 = qSketchRegion(id + "F47", true);
            var Q1;
            Q1=makeQuery(id+"F46.boolean.opBoolean","MERGE",FACE,{"derivedFrom":[makeQuery(id+"F43.boolean.opBoolean","MERGE",FACE,{"derivedFrom":[makeQuery(id+"F21.boolean.opBoolean","MERGE",FACE,{"derivedFrom":[makeQuery(id+"F19.boolean.opBoolean","MERGE",FACE,{"derivedFrom":[makeQuery(id+"F17.boolean.opBoolean","MERGE",FACE,{"derivedFrom":[makeQuery(id+"F15.boolean.opBoolean","MERGE",FACE,{"derivedFrom":[makeQuery(id+"F11.boolean.opBoolean","MERGE",FACE,{"derivedFrom":[makeQuery(id+"F5.boolean.opBoolean","MERGE",FACE,{"derivedFrom":[makeQuery(id+"F3.opExtrude","CAP_FACE",FACE,{"disambiguationData":[OSD([sQuery(id+"F2.wireOp",EDGE,"E1.bottom"),sQuery(id+"F2.wireOp",EDGE,"E1.top"),sQuery(id+"F2.wireOp",EDGE,"E1.left"),sQuery(id+"F2.wireOp",EDGE,"E1.right")])],"isStart":false}),makeQuery(id+"F5.opExtrude","CAP_FACE",FACE,{"disambiguationData":[OSD([sQuery(id+"F4.wireOp",EDGE,"E2.bottom"),sQuery(id+"F4.wireOp",EDGE,"E2.top"),sQuery(id+"F4.wireOp",EDGE,"E2.left"),sQuery(id+"F4.wireOp",EDGE,"E2.right")])],"isStart":false})]}),makeQuery(id+"F11.opExtrude","CAP_FACE",FACE,{"disambiguationData":[OSD([sQuery(id+"F10.wireOp",EDGE,"E4.bottom"),sQuery(id+"F10.wireOp",EDGE,"E4.top"),sQuery(id+"F10.wireOp",EDGE,"E4.left"),sQuery(id+"F10.wireOp",EDGE,"E4.right"),sQuery(id+"F10.wireOp",EDGE,"E5.top"),sQuery(id+"F10.wireOp",EDGE,"E5.left"),sQuery(id+"F10.wireOp",EDGE,"E5.right")])],"isStart":false})]}),makeQuery(id+"F15.opExtrude","CAP_FACE",FACE,{"disambiguationData":[OSD([sQuery(id+"F14.wireOp",EDGE,"E10.bottom"),sQuery(id+"F14.wireOp",EDGE,"E10.top"),sQuery(id+"F14.wireOp",EDGE,"E10.left"),sQuery(id+"F14.wireOp",EDGE,"E10.right")])],"isStart":false})]}),makeQuery(id+"F17.opExtrude","CAP_FACE",FACE,{"disambiguationData":[OSD([sQuery(id+"F16.wireOp",EDGE,"E11.bottom"),sQuery(id+"F16.wireOp",EDGE,"E11.top"),sQuery(id+"F16.wireOp",EDGE,"E11.left"),sQuery(id+"F16.wireOp",EDGE,"E11.right")])],"isStart":false})]}),makeQuery(id+"F19.opExtrude","CAP_FACE",FACE,{"disambiguationData":[OSD([sQuery(id+"F18.wireOp",EDGE,"E12.bottom"),sQuery(id+"F18.wireOp",EDGE,"E12.top"),sQuery(id+"F18.wireOp",EDGE,"E12.left"),sQuery(id+"F18.wireOp",EDGE,"E12.right")])],"isStart":false})]}),makeQuery(id+"F21.opExtrude","CAP_FACE",FACE,{"disambiguationData":[OSD([sQuery(id+"F20.wireOp",EDGE,"E13.bottom"),sQuery(id+"F20.wireOp",EDGE,"E13.top"),sQuery(id+"F20.wireOp",EDGE,"E13.left"),sQuery(id+"F20.wireOp",EDGE,"E13.right")])],"isStart":false})]}),makeQuery(id+"F43.opExtrude","CAP_FACE",FACE,{"disambiguationData":[OSD([sQuery(id+"F42.wireOp",EDGE,"E25.bottom"),sQuery(id+"F42.wireOp",EDGE,"E25.top"),sQuery(id+"F42.wireOp",EDGE,"E25.left"),sQuery(id+"F42.wireOp",EDGE,"E25.right")])],"isStart":false})]}),makeQuery(id+"F46.opExtrude","CAP_FACE",FACE,{"disambiguationData":[OSD([sQuery(id+"F45.wireOp",EDGE,"E26.bottom"),sQuery(id+"F45.wireOp",EDGE,"E26.top"),sQuery(id+"F45.wireOp",EDGE,"E26.left"),sQuery(id+"F45.wireOp",EDGE,"E26.right")])],"isStart":false})]});
            extrude(context, id + "F48", {"entities" : qUnion([Q0]), "operationType" : NewBodyOperationType.ADD, "endBound" : BoundingType.UP_TO_SURFACE, "depth" : 25.4 * mm, "endBoundEntityFace" : qUnion([Q1]), "offsetDistance" : 25.4 * mm});
        }
        {
            var Q0;
            Q0=makeQuery(id+"F48.boolean.opBoolean","MERGE",FACE,{"derivedFrom":[makeQuery(id+"F46.boolean.opBoolean","MERGE",FACE,{"derivedFrom":[makeQuery(id+"F43.opExtrude","SWEPT_FACE",FACE,{"disambiguationData":[OSD([sQuery(id+"F42.wireOp",EDGE,"E25.right")])]}),makeQuery(id+"F46.opExtrude","SWEPT_FACE",FACE,{"disambiguationData":[OSD([sQuery(id+"F45.wireOp",EDGE,"E26.left")])]})]}),makeQuery(id+"F48.opExtrude","SWEPT_FACE",FACE,{"disambiguationData":[OSD([sQuery(id+"F47.wireOp",EDGE,"E27.left")])]})]});
            var sketch = newSketch(context, id + "F49", { "sketchPlane" : qUnion([Q0])});
            skLineSegment(sketch, "E28.bottom", {"start": v(3460.75, 190.5) * mm, "end": v(4254.5, 190.5) * mm});
            skLineSegment(sketch, "E28.top", {"start": v(3460.75, 2209.8) * mm, "end": v(4254.5, 2209.8) * mm});
            skLineSegment(sketch, "E28.left", {"start": v(3460.75, 190.5) * mm, "end": v(3460.75, 2209.8) * mm});
            skLineSegment(sketch, "E28.right", {"start": v(4254.5, 190.5) * mm, "end": v(4254.5, 2209.8) * mm});
            skSolve(sketch);
        }
        {
            var Q0;
            Q0 = qSketchRegion(id + "F49", true);
            extrude(context, id + "F50", {"entities" : qUnion([Q0]), "operationType" : NewBodyOperationType.REMOVE, "oppositeDirection" : true, "depth" : 101.6 * mm, "offsetDistance" : 25.4 * mm});
        }
        {
            var Q0;
            {var subQ2=sQuery(id+"F36.wireOp",EDGE,"E21.top");Q0=makeQuery(id+"F44.boolean.opBoolean","MERGE",FACE,{"derivedFrom":[makeQuery(id+"F43.boolean.opBoolean","SPLIT",FACE,{"disambiguationData":[TD([makeQuery(id+"F5.opExtrude","SWEPT_FACE",FACE,{"disambiguationData":[OSD([sQuery(id+"F4.wireOp",EDGE,"E2.top")])]})])],"derivedFrom":makeQuery(id+"F37.boolean.opBoolean","MERGE",FACE,{"derivedFrom":[makeQuery(id+"F35.boolean.opBoolean","MERGE",FACE,{"derivedFrom":[makeQuery(id+"F31.opExtrude","SWEPT_FACE",FACE,{"disambiguationData":[OSD([sQuery(id+"F30.wireOp",EDGE,"E18.top")])]}),makeQuery(id+"F35.opExtrude","SWEPT_FACE",FACE,{"disambiguationData":[OSD([sQuery(id+"F34.wireOp",EDGE,"E20.top")])]})]}),makeQuery(id+"F37.opExtrude","SWEPT_FACE",FACE,{"disambiguationData":[OSD([subQ2])]})]})}),makeQuery(id+"F44.opExtrude","CAP_FACE",FACE,{"disambiguationData":[OSD([sQuery(id+"F40.wireOp",EDGE,"E23.bottom"),sQuery(id+"F40.wireOp",EDGE,"E23.top"),sQuery(id+"F40.wireOp",EDGE,"E23.left"),sQuery(id+"F40.wireOp",EDGE,"E23.right"),sQuery(id+"F40.wireOp",EDGE,"E24.bottom"),sQuery(id+"F40.wireOp",EDGE,"E24.top"),sQuery(id+"F40.wireOp",EDGE,"E24.left"),sQuery(id+"F40.wireOp",EDGE,"E24.right")])],"isStart":false})]});}
            var sketch = newSketch(context, id + "F51", { "sketchPlane" : qUnion([Q0])});
            skLineSegment(sketch, "E29.bottom", {"start": v(1752.6, -3384.55) * mm, "end": v(6534.15, -3384.55) * mm});
            skLineSegment(sketch, "E29.top", {"start": v(1752.6, -3308.35) * mm, "end": v(6534.15, -3308.35) * mm});
            skLineSegment(sketch, "E29.left", {"start": v(1752.6, -3384.55) * mm, "end": v(1752.6, -3308.35) * mm});
            skLineSegment(sketch, "E29.right", {"start": v(6534.15, -3384.55) * mm, "end": v(6534.15, -3308.35) * mm});
            skSolve(sketch);
        }
        {
            var Q0;
            Q0 = qSketchRegion(id + "F51", true);
            var Q1;
            Q1=makeQuery(id+"F48.boolean.opBoolean","MERGE",FACE,{"derivedFrom":[makeQuery(id+"F46.boolean.opBoolean","MERGE",FACE,{"derivedFrom":[makeQuery(id+"F43.boolean.opBoolean","MERGE",FACE,{"derivedFrom":[makeQuery(id+"F21.boolean.opBoolean","MERGE",FACE,{"derivedFrom":[makeQuery(id+"F19.boolean.opBoolean","MERGE",FACE,{"derivedFrom":[makeQuery(id+"F17.boolean.opBoolean","MERGE",FACE,{"derivedFrom":[makeQuery(id+"F15.boolean.opBoolean","MERGE",FACE,{"derivedFrom":[makeQuery(id+"F11.boolean.opBoolean","MERGE",FACE,{"derivedFrom":[makeQuery(id+"F5.boolean.opBoolean","MERGE",FACE,{"derivedFrom":[makeQuery(id+"F3.opExtrude","CAP_FACE",FACE,{"disambiguationData":[OSD([sQuery(id+"F2.wireOp",EDGE,"E1.bottom"),sQuery(id+"F2.wireOp",EDGE,"E1.top"),sQuery(id+"F2.wireOp",EDGE,"E1.left"),sQuery(id+"F2.wireOp",EDGE,"E1.right")])],"isStart":false}),makeQuery(id+"F5.opExtrude","CAP_FACE",FACE,{"disambiguationData":[OSD([sQuery(id+"F4.wireOp",EDGE,"E2.bottom"),sQuery(id+"F4.wireOp",EDGE,"E2.top"),sQuery(id+"F4.wireOp",EDGE,"E2.left"),sQuery(id+"F4.wireOp",EDGE,"E2.right")])],"isStart":false})]}),makeQuery(id+"F11.opExtrude","CAP_FACE",FACE,{"disambiguationData":[OSD([sQuery(id+"F10.wireOp",EDGE,"E4.bottom"),sQuery(id+"F10.wireOp",EDGE,"E4.top"),sQuery(id+"F10.wireOp",EDGE,"E4.left"),sQuery(id+"F10.wireOp",EDGE,"E4.right"),sQuery(id+"F10.wireOp",EDGE,"E5.top"),sQuery(id+"F10.wireOp",EDGE,"E5.left"),sQuery(id+"F10.wireOp",EDGE,"E5.right")])],"isStart":false})]}),makeQuery(id+"F15.opExtrude","CAP_FACE",FACE,{"disambiguationData":[OSD([sQuery(id+"F14.wireOp",EDGE,"E10.bottom"),sQuery(id+"F14.wireOp",EDGE,"E10.top"),sQuery(id+"F14.wireOp",EDGE,"E10.left"),sQuery(id+"F14.wireOp",EDGE,"E10.right")])],"isStart":false})]}),makeQuery(id+"F17.opExtrude","CAP_FACE",FACE,{"disambiguationData":[OSD([sQuery(id+"F16.wireOp",EDGE,"E11.bottom"),sQuery(id+"F16.wireOp",EDGE,"E11.top"),sQuery(id+"F16.wireOp",EDGE,"E11.left"),sQuery(id+"F16.wireOp",EDGE,"E11.right")])],"isStart":false})]}),makeQuery(id+"F19.opExtrude","CAP_FACE",FACE,{"disambiguationData":[OSD([sQuery(id+"F18.wireOp",EDGE,"E12.bottom"),sQuery(id+"F18.wireOp",EDGE,"E12.top"),sQuery(id+"F18.wireOp",EDGE,"E12.left"),sQuery(id+"F18.wireOp",EDGE,"E12.right")])],"isStart":false})]}),makeQuery(id+"F21.opExtrude","CAP_FACE",FACE,{"disambiguationData":[OSD([sQuery(id+"F20.wireOp",EDGE,"E13.bottom"),sQuery(id+"F20.wireOp",EDGE,"E13.top"),sQuery(id+"F20.wireOp",EDGE,"E13.left"),sQuery(id+"F20.wireOp",EDGE,"E13.right")])],"isStart":false})]}),makeQuery(id+"F43.opExtrude","CAP_FACE",FACE,{"disambiguationData":[OSD([sQuery(id+"F42.wireOp",EDGE,"E25.bottom"),sQuery(id+"F42.wireOp",EDGE,"E25.top"),sQuery(id+"F42.wireOp",EDGE,"E25.left"),sQuery(id+"F42.wireOp",EDGE,"E25.right")])],"isStart":false})]}),makeQuery(id+"F46.opExtrude","CAP_FACE",FACE,{"disambiguationData":[OSD([sQuery(id+"F45.wireOp",EDGE,"E26.bottom"),sQuery(id+"F45.wireOp",EDGE,"E26.top"),sQuery(id+"F45.wireOp",EDGE,"E26.left"),sQuery(id+"F45.wireOp",EDGE,"E26.right")])],"isStart":false})]}),makeQuery(id+"F48.opExtrude","CAP_FACE",FACE,{"disambiguationData":[OSD([sQuery(id+"F47.wireOp",EDGE,"E27.bottom"),sQuery(id+"F47.wireOp",EDGE,"E27.top"),sQuery(id+"F47.wireOp",EDGE,"E27.left"),sQuery(id+"F47.wireOp",EDGE,"E27.right")])],"isStart":false})]});
            extrude(context, id + "F52", {"entities" : qUnion([Q0]), "operationType" : NewBodyOperationType.ADD, "endBound" : BoundingType.UP_TO_SURFACE, "depth" : 25.4 * mm, "endBoundEntityFace" : qUnion([Q1]), "offsetDistance" : 25.4 * mm});
        }
        {
            var Q0;
            Q0=makeQuery(id+"F11.opExtrude","SWEPT_FACE",FACE,{"disambiguationData":[OSD([sQuery(id+"F10.wireOp",EDGE,"E5.right")])]});
            var sketch = newSketch(context, id + "F53", { "sketchPlane" : qUnion([Q0])});
            skLineSegment(sketch, "E30.bottom", {"start": v(2228.85, 762) * mm, "end": v(1492.25, 762) * mm});
            skLineSegment(sketch, "E30.top", {"start": v(2228.85, 2781.3) * mm, "end": v(1492.25, 2781.3) * mm});
            skLineSegment(sketch, "E30.left", {"start": v(2228.85, 762) * mm, "end": v(2228.85, 2781.3) * mm});
            skLineSegment(sketch, "E30.right", {"start": v(1492.25, 762) * mm, "end": v(1492.25, 2781.3) * mm});
            skSolve(sketch);
        }
        {
            var Q0;
            Q0 = qSketchRegion(id + "F53", true);
            extrude(context, id + "F54", {"entities" : qUnion([Q0]), "operationType" : NewBodyOperationType.REMOVE, "oppositeDirection" : true, "depth" : 101.6 * mm, "offsetDistance" : 25.4 * mm});
        }
        {
            var Q0;
            Q0=makeQuery(id+"F54.boolean.opBoolean","MERGE",FACE,{"derivedFrom":[makeQuery(id+"F9.opExtrude","CAP_FACE",FACE,{"disambiguationData":[OSD([sQuery(id+"F6.wireOp",EDGE,"E3.bottom"),sQuery(id+"F6.wireOp",EDGE,"E3.top"),sQuery(id+"F6.wireOp",EDGE,"E3.left"),sQuery(id+"F6.wireOp",EDGE,"E3.right")])],"isStart":false})],"fromTools":[makeQuery(id+"F54.opExtrude","SWEPT_FACE",FACE,{"disambiguationData":[OSD([sQuery(id+"F53.wireOp",EDGE,"E30.bottom")])]})]});
            var sketch = newSketch(context, id + "F55", { "sketchPlane" : qUnion([Q0])});
            skLineSegment(sketch, "E31.bottom", {"start": v(1651, -1397) * mm, "end": v(76.2, -1397) * mm});
            skLineSegment(sketch, "E31.top", {"start": v(1651, -1498.6) * mm, "end": v(76.2, -1498.6) * mm});
            skLineSegment(sketch, "E31.left", {"start": v(1651, -1397) * mm, "end": v(1651, -1498.6) * mm});
            skLineSegment(sketch, "E31.right", {"start": v(76.2, -1397) * mm, "end": v(76.2, -1498.6) * mm});
            skSolve(sketch);
        }
        {
            var Q0;
            Q0 = qSketchRegion(id + "F55", true);
            var Q1;
            Q1=makeQuery(id+"F52.boolean.opBoolean","MERGE",FACE,{"derivedFrom":[makeQuery(id+"F48.boolean.opBoolean","MERGE",FACE,{"derivedFrom":[makeQuery(id+"F46.boolean.opBoolean","MERGE",FACE,{"derivedFrom":[makeQuery(id+"F43.boolean.opBoolean","MERGE",FACE,{"derivedFrom":[makeQuery(id+"F21.boolean.opBoolean","MERGE",FACE,{"derivedFrom":[makeQuery(id+"F19.boolean.opBoolean","MERGE",FACE,{"derivedFrom":[makeQuery(id+"F17.boolean.opBoolean","MERGE",FACE,{"derivedFrom":[makeQuery(id+"F15.boolean.opBoolean","MERGE",FACE,{"derivedFrom":[makeQuery(id+"F11.boolean.opBoolean","MERGE",FACE,{"derivedFrom":[makeQuery(id+"F5.boolean.opBoolean","MERGE",FACE,{"derivedFrom":[makeQuery(id+"F3.opExtrude","CAP_FACE",FACE,{"disambiguationData":[OSD([sQuery(id+"F2.wireOp",EDGE,"E1.bottom"),sQuery(id+"F2.wireOp",EDGE,"E1.top"),sQuery(id+"F2.wireOp",EDGE,"E1.left"),sQuery(id+"F2.wireOp",EDGE,"E1.right")])],"isStart":false}),makeQuery(id+"F5.opExtrude","CAP_FACE",FACE,{"disambiguationData":[OSD([sQuery(id+"F4.wireOp",EDGE,"E2.bottom"),sQuery(id+"F4.wireOp",EDGE,"E2.top"),sQuery(id+"F4.wireOp",EDGE,"E2.left"),sQuery(id+"F4.wireOp",EDGE,"E2.right")])],"isStart":false})]}),makeQuery(id+"F11.opExtrude","CAP_FACE",FACE,{"disambiguationData":[OSD([sQuery(id+"F10.wireOp",EDGE,"E4.bottom"),sQuery(id+"F10.wireOp",EDGE,"E4.top"),sQuery(id+"F10.wireOp",EDGE,"E4.left"),sQuery(id+"F10.wireOp",EDGE,"E4.right"),sQuery(id+"F10.wireOp",EDGE,"E5.top"),sQuery(id+"F10.wireOp",EDGE,"E5.left"),sQuery(id+"F10.wireOp",EDGE,"E5.right")])],"isStart":false})]}),makeQuery(id+"F15.opExtrude","CAP_FACE",FACE,{"disambiguationData":[OSD([sQuery(id+"F14.wireOp",EDGE,"E10.bottom"),sQuery(id+"F14.wireOp",EDGE,"E10.top"),sQuery(id+"F14.wireOp",EDGE,"E10.left"),sQuery(id+"F14.wireOp",EDGE,"E10.right")])],"isStart":false})]}),makeQuery(id+"F17.opExtrude","CAP_FACE",FACE,{"disambiguationData":[OSD([sQuery(id+"F16.wireOp",EDGE,"E11.bottom"),sQuery(id+"F16.wireOp",EDGE,"E11.top"),sQuery(id+"F16.wireOp",EDGE,"E11.left"),sQuery(id+"F16.wireOp",EDGE,"E11.right")])],"isStart":false})]}),makeQuery(id+"F19.opExtrude","CAP_FACE",FACE,{"disambiguationData":[OSD([sQuery(id+"F18.wireOp",EDGE,"E12.bottom"),sQuery(id+"F18.wireOp",EDGE,"E12.top"),sQuery(id+"F18.wireOp",EDGE,"E12.left"),sQuery(id+"F18.wireOp",EDGE,"E12.right")])],"isStart":false})]}),makeQuery(id+"F21.opExtrude","CAP_FACE",FACE,{"disambiguationData":[OSD([sQuery(id+"F20.wireOp",EDGE,"E13.bottom"),sQuery(id+"F20.wireOp",EDGE,"E13.top"),sQuery(id+"F20.wireOp",EDGE,"E13.left"),sQuery(id+"F20.wireOp",EDGE,"E13.right")])],"isStart":false})]}),makeQuery(id+"F43.opExtrude","CAP_FACE",FACE,{"disambiguationData":[OSD([sQuery(id+"F42.wireOp",EDGE,"E25.bottom"),sQuery(id+"F42.wireOp",EDGE,"E25.top"),sQuery(id+"F42.wireOp",EDGE,"E25.left"),sQuery(id+"F42.wireOp",EDGE,"E25.right")])],"isStart":false})]}),makeQuery(id+"F46.opExtrude","CAP_FACE",FACE,{"disambiguationData":[OSD([sQuery(id+"F45.wireOp",EDGE,"E26.bottom"),sQuery(id+"F45.wireOp",EDGE,"E26.top"),sQuery(id+"F45.wireOp",EDGE,"E26.left"),sQuery(id+"F45.wireOp",EDGE,"E26.right")])],"isStart":false})]}),makeQuery(id+"F48.opExtrude","CAP_FACE",FACE,{"disambiguationData":[OSD([sQuery(id+"F47.wireOp",EDGE,"E27.bottom"),sQuery(id+"F47.wireOp",EDGE,"E27.top"),sQuery(id+"F47.wireOp",EDGE,"E27.left"),sQuery(id+"F47.wireOp",EDGE,"E27.right")])],"isStart":false})]}),makeQuery(id+"F52.opExtrude","CAP_FACE",FACE,{"disambiguationData":[OSD([sQuery(id+"F51.wireOp",EDGE,"E29.bottom"),sQuery(id+"F51.wireOp",EDGE,"E29.top"),sQuery(id+"F51.wireOp",EDGE,"E29.left"),sQuery(id+"F51.wireOp",EDGE,"E29.right")])],"isStart":false})]});
            extrude(context, id + "F56", {"entities" : qUnion([Q0]), "operationType" : NewBodyOperationType.ADD, "endBound" : BoundingType.UP_TO_SURFACE, "depth" : 25.4 * mm, "endBoundEntityFace" : qUnion([Q1]), "offsetDistance" : 25.4 * mm});
        }
        {
            var Q0;
            {var subQ0=sQuery(id+"F10.wireOp",EDGE,"E5.right");var subQ1=sQuery(id+"F4.wireOp",EDGE,"E2.top");Q0=makeQuery(id+"F56.boolean.opBoolean","SPLIT",FACE,{"disambiguationData":[TD([makeQuery(id+"F5.opExtrude","SWEPT_FACE",FACE,{"disambiguationData":[OSD([subQ1])]})])],"derivedFrom":makeQuery(id+"F11.opExtrude","SWEPT_FACE",FACE,{"disambiguationData":[OSD([subQ0])]})});}
            var sketch = newSketch(context, id + "F57", { "sketchPlane" : qUnion([Q0])});
            skLineSegment(sketch, "E32.bottom", {"start": v(558.8, 762) * mm, "end": v(1295.4, 762) * mm});
            skLineSegment(sketch, "E32.top", {"start": v(558.8, 2781.3) * mm, "end": v(1295.4, 2781.3) * mm});
            skLineSegment(sketch, "E32.left", {"start": v(558.8, 762) * mm, "end": v(558.8, 2781.3) * mm});
            skLineSegment(sketch, "E32.right", {"start": v(1295.4, 762) * mm, "end": v(1295.4, 2781.3) * mm});
            skSolve(sketch);
        }
        {
            var Q0;
            Q0 = qSketchRegion(id + "F57", true);
            extrude(context, id + "F58", {"entities" : qUnion([Q0]), "operationType" : NewBodyOperationType.REMOVE, "oppositeDirection" : true, "depth" : 101.6 * mm, "offsetDistance" : 25.4 * mm});
        }
        {
            var Q0;
            Q0=makeQuery(id+"F58.boolean.opBoolean","MERGE",FACE,{"derivedFrom":[makeQuery(id+"F56.boolean.opBoolean","SPLIT",FACE,{"disambiguationData":[TD([makeQuery(id+"F5.opExtrude","SWEPT_FACE",FACE,{"disambiguationData":[OSD([sQuery(id+"F4.wireOp",EDGE,"E2.top")])]})])],"derivedFrom":makeQuery(id+"F54.boolean.opBoolean","MERGE",FACE,{"derivedFrom":[makeQuery(id+"F9.opExtrude","CAP_FACE",FACE,{"disambiguationData":[OSD([sQuery(id+"F6.wireOp",EDGE,"E3.bottom"),sQuery(id+"F6.wireOp",EDGE,"E3.top"),sQuery(id+"F6.wireOp",EDGE,"E3.left"),sQuery(id+"F6.wireOp",EDGE,"E3.right")])],"isStart":false})],"fromTools":[makeQuery(id+"F54.opExtrude","SWEPT_FACE",FACE,{"disambiguationData":[OSD([sQuery(id+"F53.wireOp",EDGE,"E30.bottom")])]})]})})],"fromTools":[makeQuery(id+"F58.opExtrude","SWEPT_FACE",FACE,{"disambiguationData":[OSD([sQuery(id+"F57.wireOp",EDGE,"E32.bottom")])]})]});
            var sketch = newSketch(context, id + "F59", { "sketchPlane" : qUnion([Q0])});
            skLineSegment(sketch, "E33.bottom", {"start": v(1016, -76.2) * mm, "end": v(1625.6, -76.2) * mm});
            skLineSegment(sketch, "E33.top", {"start": v(1016, -558.8) * mm, "end": v(1625.6, -558.8) * mm});
            skLineSegment(sketch, "E33.left", {"start": v(1016, -76.2) * mm, "end": v(1016, -558.8) * mm});
            skLineSegment(sketch, "E33.right", {"start": v(1625.6, -76.2) * mm, "end": v(1625.6, -558.8) * mm});
            skSolve(sketch);
        }
        {
            var Q0;
            Q0 = qSketchRegion(id + "F59", true);
            extrude(context, id + "F60", {"entities" : qUnion([Q0]), "operationType" : NewBodyOperationType.ADD, "depth" : 863.6 * mm, "offsetDistance" : 25.4 * mm});
        }
    });
